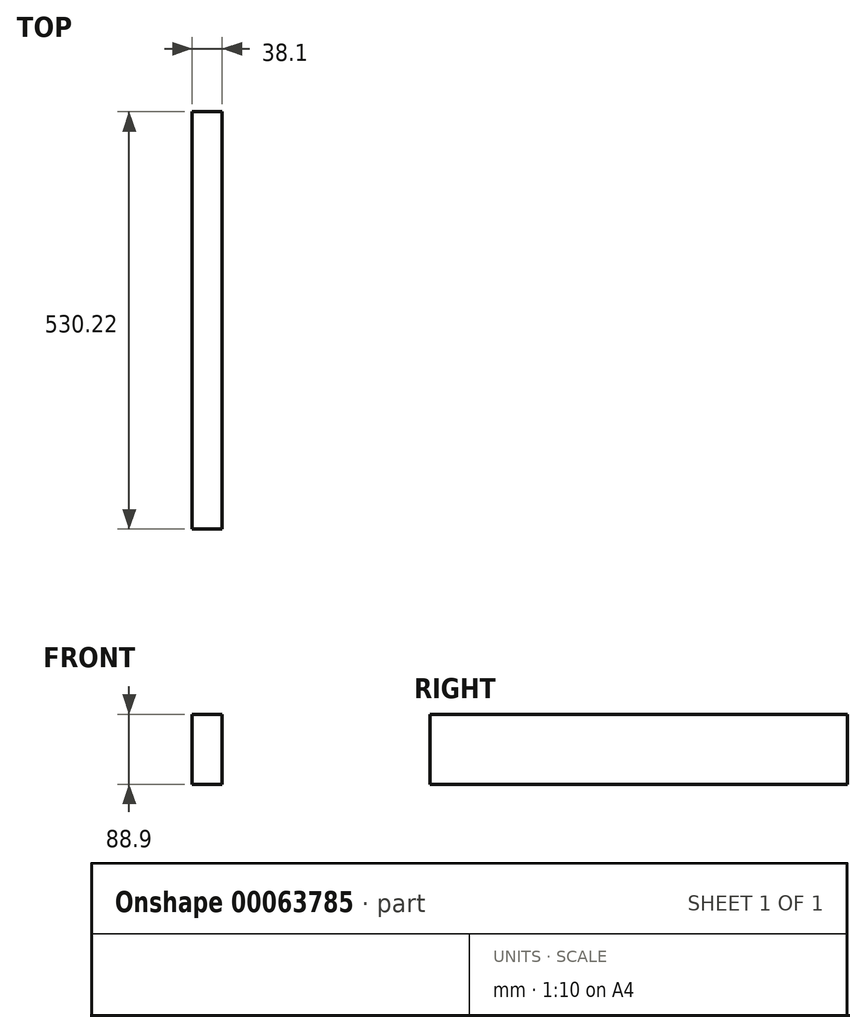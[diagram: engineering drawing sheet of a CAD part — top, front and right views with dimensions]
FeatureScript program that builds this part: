
annotation { "Feature Type Name" : "Feature", "Feature Type Description" : "" }
export const myFeature = defineFeature(function(context is Context, id is Id, definition is map)
    precondition{}
    {
        {
            var Q0;
            Q0=qCreatedBy(makeId("Front.planeOp"),FACE);
            var sketch = newSketch(context, id + "F0", { "sketchPlane" : qUnion([Q0])});
            skLineSegment(sketch, "E0.bottom", {"start": v(-18, 55.77) * mm, "end": v(20.1, 55.77) * mm});
            skLineSegment(sketch, "E0.top", {"start": v(-18, -33.13) * mm, "end": v(20.1, -33.13) * mm});
            skLineSegment(sketch, "E0.left", {"start": v(-18, 55.77) * mm, "end": v(-18, -33.13) * mm});
            skLineSegment(sketch, "E0.right", {"start": v(20.1, 55.77) * mm, "end": v(20.1, -33.13) * mm});
            skSolve(sketch);
        }
        {
            var Q0;
            Q0=qSketchRegion(id+"F0",true);
            extrude(context, id + "F1", {"entities" : qUnion([Q0]), "endBound" : BoundingType.SYMMETRIC, "depth" : 530.23 * mm});
        }
    });
